# Revit family: Motus Floor-1 BL 800 940-927 D2W BAS EU_Unhosted
name_source: partatom
category: Lighting Fixtures
revit_build: Autodesk Revit 2016 (Build: 20151007_0715(x64)
units: mm (PartAtom-declared; Revit-internal decimal feet)

## family parameters
Always vertical = Yes
Cut with Voids When Loaded = No
Light Source = Yes
OmniClass Number = 23.80.70.00
OmniClass Title = Lighting
Part Type = Normal
Room Calculation Point = No
Round Connector Dimension = Use Diameter
Shared = No
Work Plane-Based = No

## types (1)
- Motus Floor-1 BL 800 940-927 D2W BAS EU_Unhosted
    #Tubes = 1
    Apparent Load = 9 VA
    ArticleNumber = MOT028538
    Body Material and Colour = Default
    Color Filter = 16777215
    Description = Motus Floor-1 BL 800 940-927 D2W BAS EU
    Dimming Lamp Color Temperature Shift = <None>
    EANNo = 7040670285386
    Emit Shape Visible in Rendering = No
    Emit from Circle Diameter = 79 mm
    Expired = 0
    Frequency = 50 Hz
    FrequencyMax = 60 Hz
    Glamox Category = Architectural
    Glamox Family = Motus Floor
    Glamox Mounting = Floor
    GlobalTradeItemNumber = 7040670285386
    Height = 1054 mm  [stored 3.45801 ft]
    IFC Classification = Light Fixture
    IPClass = 20
    IP_Code = 20
    Lamp = LED
    Lamp Wattage = 8 W
    Length = 220 mm
    LightFixtureMountingType = FREESTANDING
    LightFixturePlacingType = FLOOR
    LumDiameter = 79 mm
    MFArtNo = MOT028538
    MaintenanceFactor = 0
    Manufacturer = Glamox
    Maximum TA = 25
    ModelLabel = Motus Floor-1 BL 800 940-927 D2W BAS EU
    ModelReference = Motus Floor
    NominalFrequencyRange = 50 Hz
    Number of Poles = 1
    NumberOfSources = 1
    Optic = SYM
    Photometric Web File = MOTUS-FLOOR-1-800-D2W.ies
    Plug Type = EU
    Power Factor = 0.98
    PowerFactor = 98.00%
    RatedVoltage = 100 V
    Specification = Architectural luminaires, for Floor mounting, IP20, light source LED, lumen out 810lm, 1x8W, ballast type AC/DC = alternating current/ direct current , with light source type Dim to warm (4000K-2700K; CRI<90), 1.4 metre cable, with EU plug, optic type SYM = Symmetric.
    Suspension Material = Default
    Tilt Angle = 90.00°
    Total Load = 8 W
    TotalWattage = 8 W
    TypeOfBallast = AC/DC = alternating current/ direct current
    URL Denmark = http://glamox.com
    URL Estonia = http://glamox.com
    URL Finland = http://glamox.com
    URL Germany = http://glamox.com
    URL Ireland = http://glamox.com
    URL Norway = http://glamox.com
    URL Other = http://glamox.com
    URL Russia = http://glamox.com
    URL Sweden = http://glamox.com
    URL UK = http://glamox.com
    UpdateDate = 20.02.2021 00:07:56
    Voltage = 100 V
    VoltageMax = 240 V
    Width = 193 mm  [stored 0.633202 ft]

note: [stored X ft] marks values corroborated as IEEE doubles in the binary element streams (Revit-internal decimal feet)

## geometry (parser evidence)
native form markers: Blend x8, Sweep x1
no freeform markers — native parametric forms only
